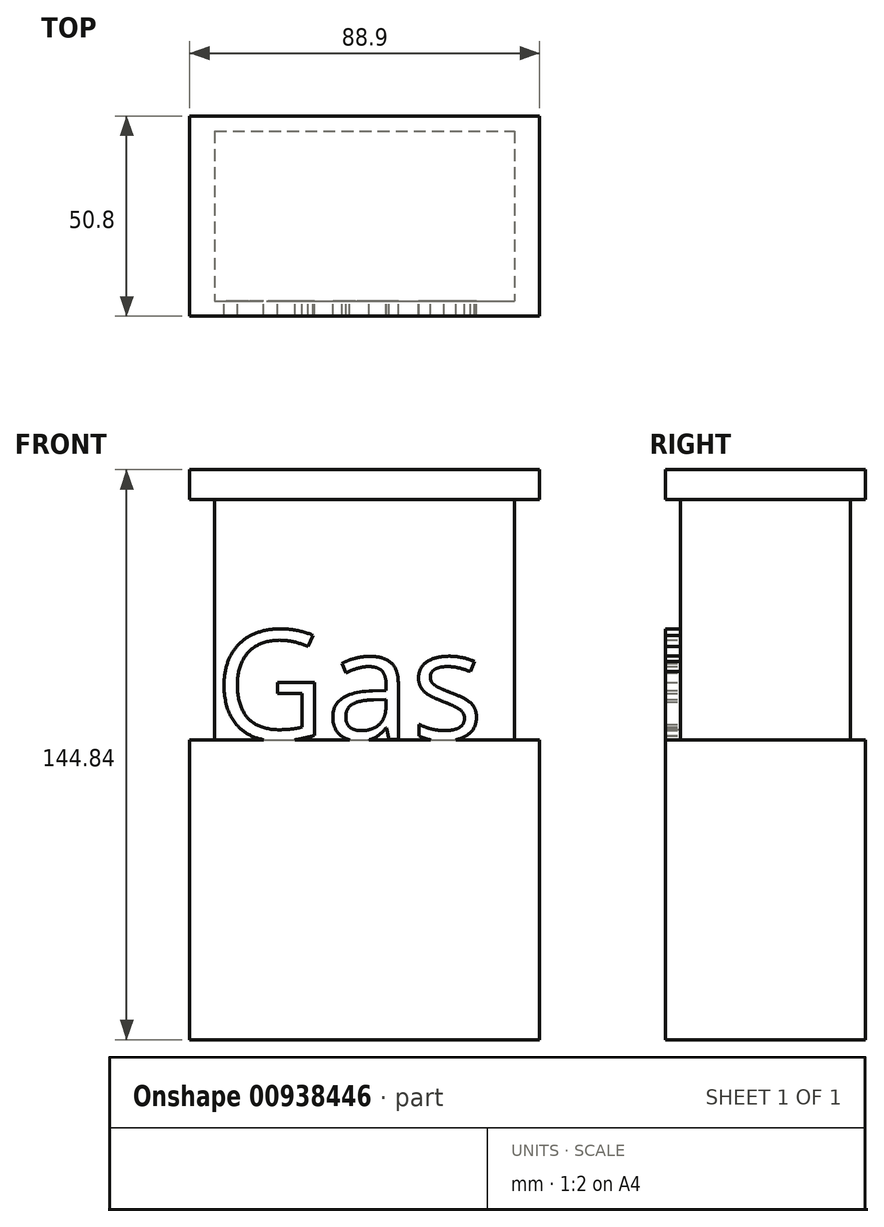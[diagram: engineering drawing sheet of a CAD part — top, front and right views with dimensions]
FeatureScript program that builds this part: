
annotation { "Feature Type Name" : "Feature", "Feature Type Description" : "" }
export const myFeature = defineFeature(function(context is Context, id is Id, definition is map)
    precondition{}
    {
        {
            var Q0;
            Q0=qCreatedBy(makeId("Top.planeOp"),FACE);
            var sketch = newSketch(context, id + "F0", { "sketchPlane" : qUnion([Q0])});
            skLineSegment(sketch, "E0.bottom", {"start": v(-44.45, 25.4) * mm, "end": v(44.45, 25.4) * mm});
            skLineSegment(sketch, "E0.top", {"start": v(-44.45, -25.4) * mm, "end": v(44.45, -25.4) * mm});
            skLineSegment(sketch, "E0.left", {"start": v(-44.45, 25.4) * mm, "end": v(-44.45, -25.4) * mm});
            skLineSegment(sketch, "E0.right", {"start": v(44.45, 25.4) * mm, "end": v(44.45, -25.4) * mm});
            skPoint(sketch, "E0.middle", {"position": v(0, 0) * mm});
            skLineSegment(sketch, "E1.bottom", {"start": v(-38.1, 21.59) * mm, "end": v(38.1, 21.59) * mm});
            skLineSegment(sketch, "E1.top", {"start": v(-38.1, -21.59) * mm, "end": v(38.1, -21.59) * mm});
            skLineSegment(sketch, "E1.left", {"start": v(-38.1, 21.59) * mm, "end": v(-38.1, -21.59) * mm});
            skLineSegment(sketch, "E1.right", {"start": v(38.1, 21.59) * mm, "end": v(38.1, -21.59) * mm});
            skLineSegment(sketch, "E2.bottom", {"start": v(-46.99, 27.94) * mm, "end": v(47, 27.94) * mm});
            skLineSegment(sketch, "E2.top", {"start": v(-47, -27.94) * mm, "end": v(46.99, -27.94) * mm});
            skLineSegment(sketch, "E2.left", {"start": v(-46.99, 27.94) * mm, "end": v(-47, -27.94) * mm});
            skLineSegment(sketch, "E2.right", {"start": v(47, 27.94) * mm, "end": v(46.99, -27.94) * mm});
            skSolve(sketch);
        }
        {
            var Q0;
            Q0=makeQuery(id+"F0.imprint","IMPRINT",FACE,{"disambiguationData":[TD([[makeQuery(id+"F0.imprint","IMPRINT",EDGE,{"derivedFrom":sQuery(id+"F0.wireOp",EDGE,"E0.bottom")}),-1.0]])]});
            extrude(context, id + "F1", {"entities" : qUnion([Q0]), "depth" : 76.2 * mm, "offsetDistance" : 25.4 * mm});
        }
        {
            var Q0;
            Q0=makeQuery(id+"F0.imprint","IMPRINT",FACE,{"disambiguationData":[TD([[makeQuery(id+"F0.imprint","IMPRINT",EDGE,{"derivedFrom":sQuery(id+"F0.wireOp",EDGE,"E1.bottom")}),-1.0]])]});
            extrude(context, id + "F2", {"entities" : qUnion([Q0]), "operationType" : NewBodyOperationType.ADD, "depth" : 140.97 * mm, "offsetDistance" : 25.4 * mm});
        }
        {
            var Q0;
            Q0=qCreatedBy(makeId("Front.planeOp"),FACE);
            var sketch = newSketch(context, id + "F3", { "sketchPlane" : qUnion([Q0])});
            skLineSegment(sketch, "E3.bottom", {"start": v(-44.45, 144.84) * mm, "end": v(44.45, 144.84) * mm});
            skLineSegment(sketch, "E3.top", {"start": v(-44.45, 137.22) * mm, "end": v(44.45, 137.22) * mm});
            skLineSegment(sketch, "E3.left", {"start": v(-44.45, 144.84) * mm, "end": v(-44.45, 137.22) * mm});
            skLineSegment(sketch, "E3.right", {"start": v(44.45, 144.84) * mm, "end": v(44.45, 137.22) * mm});
            skPoint(sketch, "E3.middle", {"position": v(0, 141.03) * mm});
            skText(sketch, "E4", { "text": "Gas ", "fontName": "OpenSans-Regular.ttf"});
            const initialGuessF3  = {"E4": [-0.03812, 0.0763, 1, 0, 0.02791]};
            skSetInitialGuess(sketch, initialGuessF3);
            skSolve(sketch);
        }
        {
            var Q0;
            Q0=makeQuery(id+"F3.imprint","IMPRINT",FACE,{"disambiguationData":[TD([[makeQuery(id+"F3.imprint","IMPRINT",EDGE,{"derivedFrom":sQuery(id+"F3.wireOp",EDGE,"E3.bottom")}),-1.0]])]});
            extrude(context, id + "F4", {"entities" : qUnion([Q0]), "operationType" : NewBodyOperationType.ADD, "endBound" : BoundingType.SYMMETRIC, "depth" : 50.8 * mm, "offsetDistance" : 25.4 * mm});
        }
        {
            var Q0;
            Q0 = qSketchRegion(id + "F3", true);
            extrude(context, id + "F5", {"entities" : qUnion([Q0]), "operationType" : NewBodyOperationType.ADD, "depth" : 25.4 * mm, "offsetDistance" : 25.4 * mm});
        }
        {
            var Q0;
            Q0=qCreatedBy(makeId("Right.planeOp"),FACE);
            var sketch = newSketch(context, id + "F6", { "sketchPlane" : qUnion([Q0])});
            skLineSegment(sketch, "E5.bottom", {"start": v(3.8, 44.4) * mm, "end": v(-3.81, 44.4) * mm});
            skLineSegment(sketch, "E5.top", {"start": v(3.8, 24.45) * mm, "end": v(-3.81, 24.45) * mm});
            skLineSegment(sketch, "E5.left", {"start": v(3.8, 44.4) * mm, "end": v(3.8, 24.45) * mm});
            skLineSegment(sketch, "E5.right", {"start": v(-3.81, 44.4) * mm, "end": v(-3.81, 24.45) * mm});
            skPoint(sketch, "E5.middle", {"position": v(0, 34.42) * mm});
            skSolve(sketch);
        }
        {
            var Q0;
            Q0=sQuery(id+"F6.wireOp",EDGE,"E5.left");
            var Q1;
            Q1=sQuery(id+"F6.wireOp",EDGE,"E5.top");
            var Q2;
            Q2=sQuery(id+"F6.wireOp",EDGE,"E5.right");
            var Q3;
            Q3=sQuery(id+"F6.wireOp",EDGE,"E5.bottom");
            extrude(context, id + "F7", {"bodyType" : ToolBodyType.SURFACE, "surfaceEntities" : qUnion([Q0, Q1, Q2, Q3]), "endBound" : BoundingType.SYMMETRIC, "depth" : 101.6 * mm, "offsetDistance" : 25.4 * mm});
        }
    });
